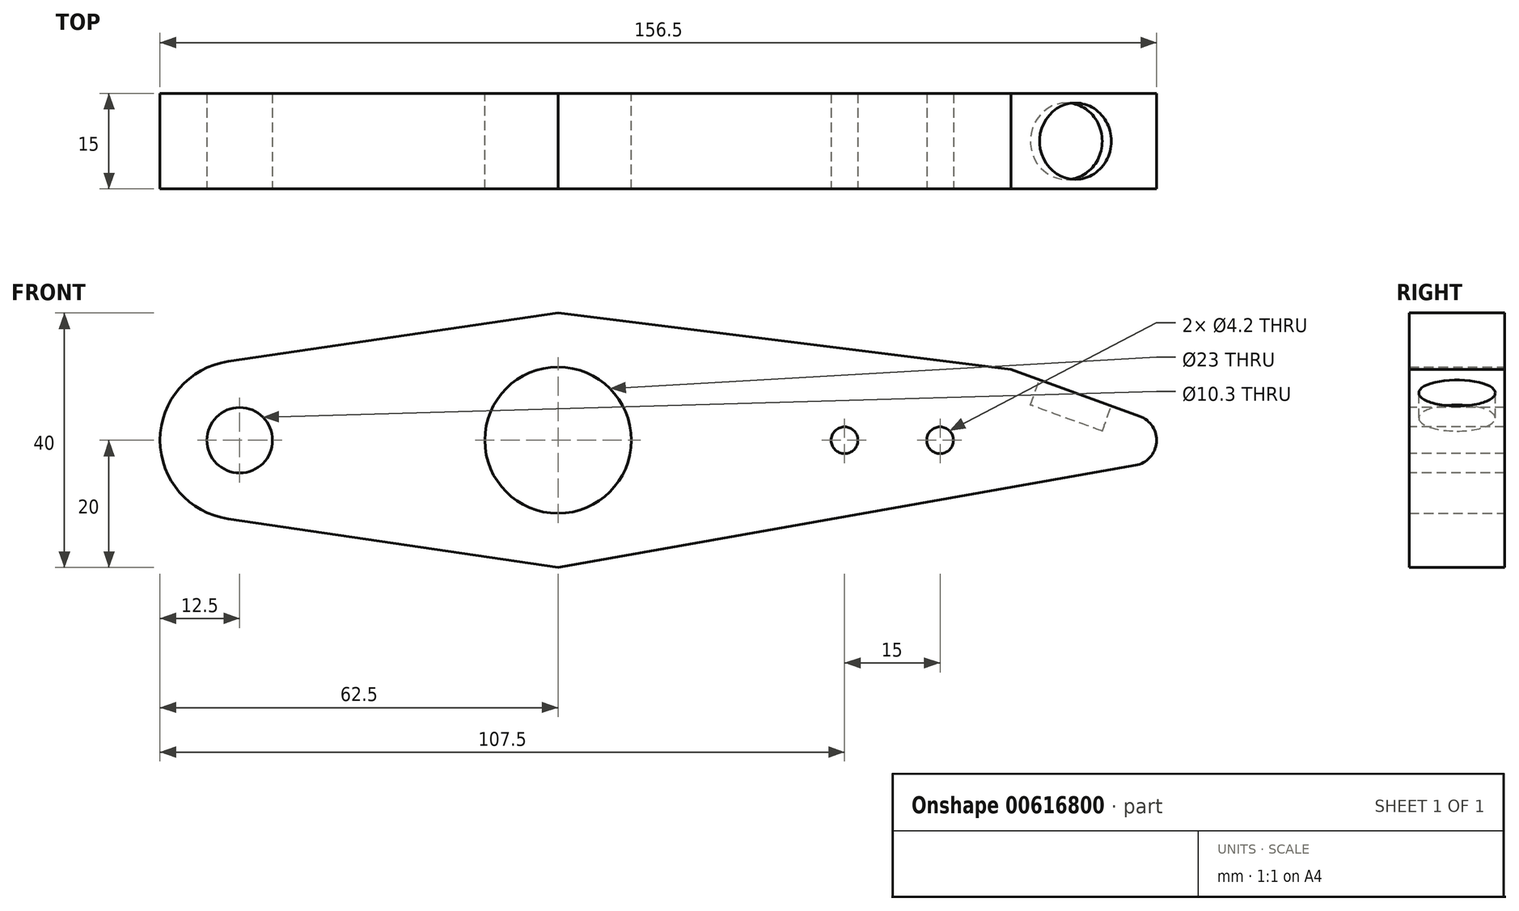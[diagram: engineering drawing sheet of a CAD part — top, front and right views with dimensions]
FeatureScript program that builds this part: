
annotation { "Feature Type Name" : "Feature", "Feature Type Description" : "" }
export const myFeature = defineFeature(function(context is Context, id is Id, definition is map)
    precondition{}
    {
        {
            var Q0;
            Q0=qCreatedBy(makeId("Front.planeOp"),FACE);
            var sketch = newSketch(context, id + "F0", { "sketchPlane" : qUnion([Q0])});
            skCircle(sketch, "E0", {"center": v(0, 0) * mm, "radius": 11.5 * mm});
            skCircle(sketch, "E1", {"center": v(-50, 0) * mm, "radius": 6 * mm, "construction": true});
            skCircle(sketch, "E2", {"center": v(45, 0) * mm, "radius": 2.5 * mm, "construction": true});
            skCircle(sketch, "E3", {"center": v(60, 0) * mm, "radius": 2.5 * mm, "construction": true});
            skLineSegment(sketch, "E4", {"start": v(0, 20) * mm, "end": v(-51.82, 12.37) * mm});
            skArc(sketch, "E5", {"start": v(-51.82, 12.37) * mm, "mid": v(-62.5, 0) * mm, "end": v(-51.82, -12.37) * mm});
            skLineSegment(sketch, "E6", {"start": v(-51.82, -12.37) * mm, "end": v(0, -20) * mm});
            skLineSegment(sketch, "E7", {"start": v(0, -20) * mm, "end": v(90.7, -3.94) * mm});
            skArc(sketch, "E8", {"start": v(90.7, -3.94) * mm, "mid": v(93.99, -0.35) * mm, "end": v(91.37, 3.76) * mm});
            skLineSegment(sketch, "E9", {"start": v(91.37, 3.76) * mm, "end": v(71.16, 11.1) * mm});
            skLineSegment(sketch, "E10", {"start": v(71.16, 11.1) * mm, "end": v(0, 20) * mm});
            skLineSegment(sketch, "E11", {"start": v(90.63, -9.98) * mm, "end": v(99.74, 15.11) * mm, "construction": true});
            skPoint(sketch, "E12", {"position": v(81.26, 7.43) * mm});
            skSolve(sketch);
        }
        {
            var Q0;
            Q0=makeQuery(id+"F0.imprint","IMPRINT",FACE,{"disambiguationData":[TD([[makeQuery(id+"F0.imprint","IMPRINT",EDGE,{"derivedFrom":sQuery(id+"F0.wireOp",EDGE,"E0")}),-1.0]])]});
            extrude(context, id + "F1", {"entities" : qUnion([Q0]), "depth" : 15 * mm, "offsetDistance" : 25 * mm});
        }
        {
            var Q0;
            Q0=makeQuery(id+"F1.opExtrude","CAP_FACE",FACE,{"disambiguationData":[OSD([sQuery(id+"F0.wireOp",EDGE,"E0"),sQuery(id+"F0.wireOp",EDGE,"E4"),sQuery(id+"F0.wireOp",EDGE,"E5"),sQuery(id+"F0.wireOp",EDGE,"E6"),sQuery(id+"F0.wireOp",EDGE,"E7"),sQuery(id+"F0.wireOp",EDGE,"E8"),sQuery(id+"F0.wireOp",EDGE,"E9"),sQuery(id+"F0.wireOp",EDGE,"E10")])],"isStart":true});
            var sketch = newSketch(context, id + "F2", { "sketchPlane" : qUnion([Q0])});
            skPoint(sketch, "E13.0", {"position": v(-60, 0) * mm});
            skPoint(sketch, "E14.0", {"position": v(-45, 0) * mm});
            skPoint(sketch, "E15.0", {"position": v(50, 0) * mm});
            skSolve(sketch);
        }
        {
            var Q0;
            Q0=sQuery(id+"F2.wireOp",VERTEX,"E13.0");
            var Q1;
            Q1=sQuery(id+"F2.wireOp",VERTEX,"E14.0");
            var Q2;
            Q2=makeQuery(id+"F1.opExtrude","SWEPT_BODY",BODY,{"disambiguationData":[OSD([sQuery(id+"F0.wireOp",EDGE,"E0"),sQuery(id+"F0.wireOp",EDGE,"E4"),sQuery(id+"F0.wireOp",EDGE,"E5"),sQuery(id+"F0.wireOp",EDGE,"E6"),sQuery(id+"F0.wireOp",EDGE,"E7"),sQuery(id+"F0.wireOp",EDGE,"E8"),sQuery(id+"F0.wireOp",EDGE,"E9"),sQuery(id+"F0.wireOp",EDGE,"E10")])]});
            hole(context, id + "F3", {"style" : HoleStyle.SIMPLE, "endStyle" : HoleEndStyle.THROUGH, "standardTappedOrClearance" : lookupTablePath({ "standard" : "ISO", "engagement" : "75%", "pitch" : "0.8 mm", "size" : "M5", "type" : "Tapped" }), "standardBlindInLast" : lookupTablePath({ "standard" : "ISO", "engagement" : "75%", "pitch" : "0.8 mm", "size" : "M5", "type" : "Tapped" }), "holeDiameter" : 4.2 * mm, "majorDiameter" : 5 * mm, "showTappedDepth" : true, "isTappedThrough" : true, "tappedDepth" : 12 * mm, "tapClearance" : 3, "locations" : qUnion([Q0, Q1]), "scope" : qUnion([Q2]), "startStyle" : HoleStartStyle.PART});
        }
        {
            var Q0;
            Q0=sQuery(id+"F0.wireOp",VERTEX,"E1.center");
            var Q1;
            Q1=makeQuery(id+"F1.opExtrude","SWEPT_BODY",BODY,{"disambiguationData":[OSD([sQuery(id+"F0.wireOp",EDGE,"E0"),sQuery(id+"F0.wireOp",EDGE,"E4"),sQuery(id+"F0.wireOp",EDGE,"E5"),sQuery(id+"F0.wireOp",EDGE,"E6"),sQuery(id+"F0.wireOp",EDGE,"E7"),sQuery(id+"F0.wireOp",EDGE,"E8"),sQuery(id+"F0.wireOp",EDGE,"E9"),sQuery(id+"F0.wireOp",EDGE,"E10")])]});
            hole(context, id + "F4", {"style" : HoleStyle.SIMPLE, "endStyle" : HoleEndStyle.THROUGH, "oppositeDirection" : true, "standardTappedOrClearance" : lookupTablePath({ "standard" : "ISO", "engagement" : "75%", "pitch" : "1.75 mm", "size" : "M12", "type" : "Tapped" }), "standardBlindInLast" : lookupTablePath({ "standard" : "ISO", "engagement" : "75%", "pitch" : "1.75 mm", "size" : "M12", "type" : "Tapped" }), "holeDiameter" : 10.3 * mm, "majorDiameter" : 12 * mm, "showTappedDepth" : true, "isTappedThrough" : true, "tappedDepth" : 12 * mm, "tapClearance" : 3, "locations" : qUnion([Q0]), "scope" : qUnion([Q1]), "startStyle" : HoleStartStyle.PART});
        }
        {
            var Q0;
            Q0=makeQuery(id+"F1.opExtrude","SWEPT_FACE",FACE,{"disambiguationData":[OSD([sQuery(id+"F0.wireOp",EDGE,"E9")])]});
            var sketch = newSketch(context, id + "F5", { "sketchPlane" : qUnion([Q0])});
            skLineSegment(sketch, "E16", {"start": v(63.1, -7.5) * mm, "end": v(84.6, -7.5) * mm, "construction": true});
            skLineSegment(sketch, "E17", {"start": v(73.84, 0) * mm, "end": v(73.84, -15) * mm, "construction": true});
            skCircle(sketch, "E18", {"center": v(73.84, -7.5) * mm, "radius": 6 * mm});
            skSolve(sketch);
        }
        {
            var Q0;
            Q0=makeQuery(id+"F5.imprint","IMPRINT",FACE,{"disambiguationData":[TD([[makeQuery(id+"F5.imprint","IMPRINT",EDGE,{"derivedFrom":sQuery(id+"F5.wireOp",EDGE,"E18")}),1.0]])]});
            extrude(context, id + "F6", {"entities" : qUnion([Q0]), "operationType" : NewBodyOperationType.REMOVE, "oppositeDirection" : true, "depth" : 4.2 * mm, "offsetDistance" : 25 * mm});
        }
    });
